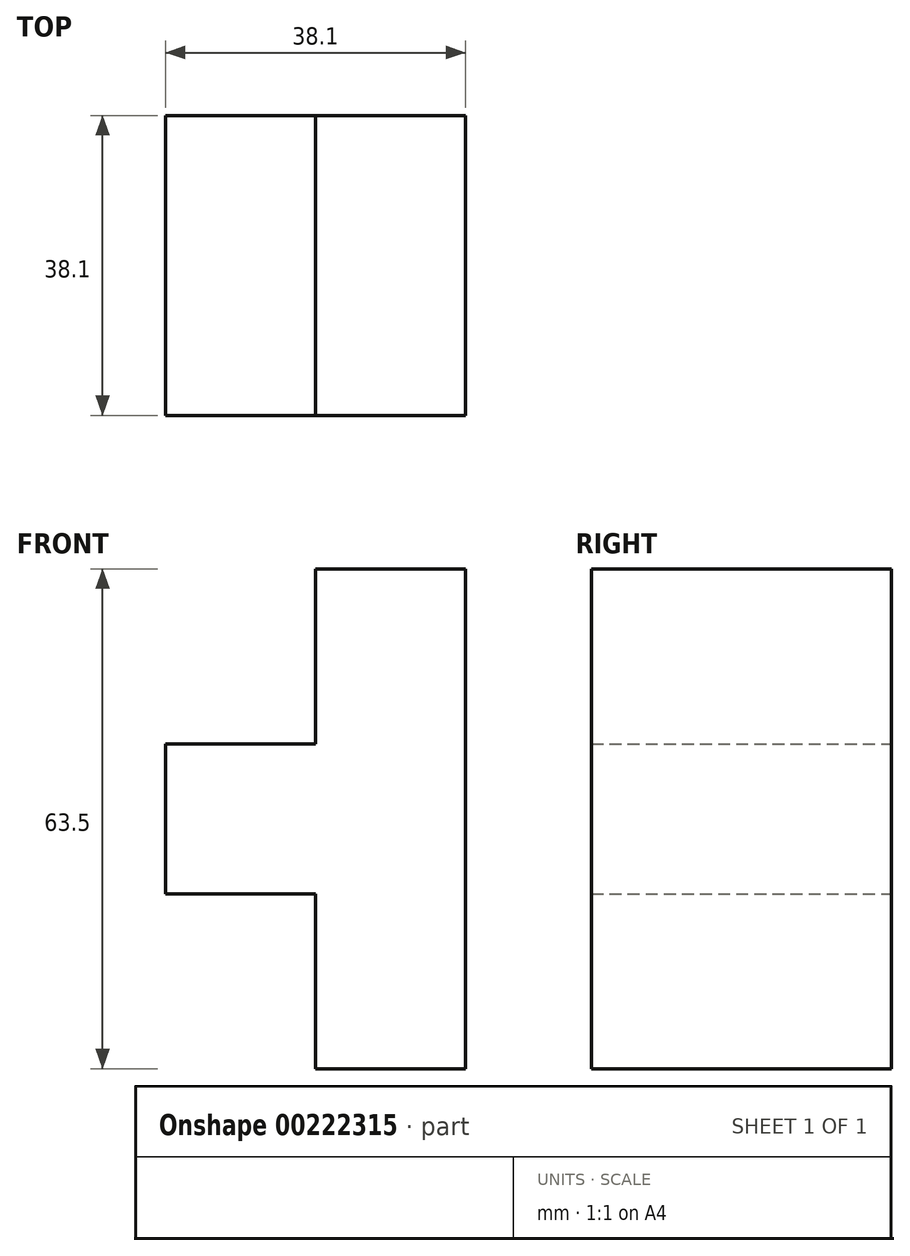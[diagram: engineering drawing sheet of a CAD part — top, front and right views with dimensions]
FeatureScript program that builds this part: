
annotation { "Feature Type Name" : "Feature", "Feature Type Description" : "" }
export const myFeature = defineFeature(function(context is Context, id is Id, definition is map)
    precondition{}
    {
        {
            var Q0;
            Q0=qCreatedBy(makeId("Front.planeOp"),FACE);
            var sketch = newSketch(context, id + "F0", { "sketchPlane" : qUnion([Q0])});
            skLineSegment(sketch, "E0.bottom", {"start": v(-52.64, 2.27) * mm, "end": v(-71.69, 2.27) * mm});
            skLineSegment(sketch, "E0.top", {"start": v(-52.64, 65.77) * mm, "end": v(-71.69, 65.77) * mm});
            skLineSegment(sketch, "E0.left", {"start": v(-52.64, 2.27) * mm, "end": v(-52.64, 65.77) * mm});
            skLineSegment(sketch, "E0.right", {"start": v(-71.69, 2.27) * mm, "end": v(-71.69, 65.77) * mm});
            skPoint(sketch, "E0.middle", {"position": v(-62.16, 34.02) * mm});
            skLineSegment(sketch, "E1.bottom", {"start": v(-71.69, 24.5) * mm, "end": v(-90.74, 24.5) * mm});
            skLineSegment(sketch, "E1.top", {"start": v(-71.69, 43.55) * mm, "end": v(-90.74, 43.55) * mm});
            skLineSegment(sketch, "E1.left", {"start": v(-71.69, 24.5) * mm, "end": v(-71.69, 43.55) * mm});
            skLineSegment(sketch, "E1.right", {"start": v(-90.74, 24.5) * mm, "end": v(-90.74, 43.55) * mm});
            skPoint(sketch, "E1.middle", {"position": v(-81.21, 34.02) * mm});
            skPoint(sketch, "E1.middle.positionSnap0", {"position": v(-71.69, 34.02) * mm});
            skPoint(sketch, "E1.centerSnap0", {"position": v(-71.69, 34.02) * mm});
            skSolve(sketch);
        }
        {
            var Q0;
            Q0=qSketchRegion(id+"F0",true);
            extrude(context, id + "F1", {"entities" : qUnion([Q0]), "depth" : 25.4 * mm});
        }
        {
            var Q0;
            Q0=qSketchRegion(id+"F0",true);
            extrude(context, id + "F2", {"entities" : qUnion([Q0]), "operationType" : NewBodyOperationType.ADD, "endBound" : BoundingType.SYMMETRIC, "depth" : 25.4 * mm});
        }
    });
